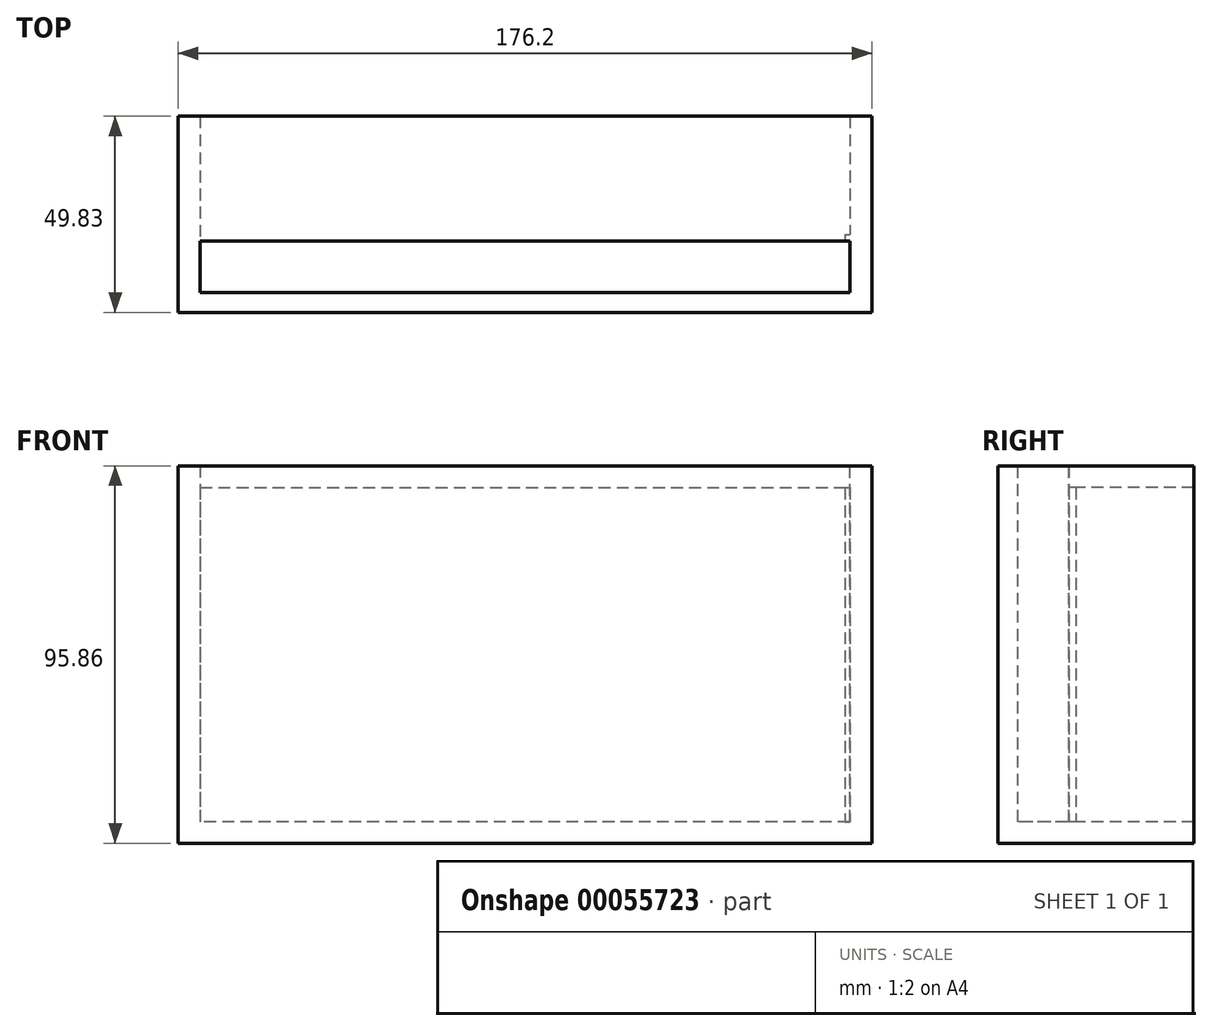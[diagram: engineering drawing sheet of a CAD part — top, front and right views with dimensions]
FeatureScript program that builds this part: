
annotation { "Feature Type Name" : "Feature", "Feature Type Description" : "" }
export const myFeature = defineFeature(function(context is Context, id is Id, definition is map)
    precondition{}
    {
        {
            var Q0;
            Q0=qCreatedBy(makeId("Front.planeOp"),FACE);
            var sketch = newSketch(context, id + "F0", { "sketchPlane" : qUnion([Q0])});
            skLineSegment(sketch, "E0.rect.bottom", {"start": v(82.5, 42.5) * mm, "end": v(-82.5, 42.5) * mm});
            skLineSegment(sketch, "E0.rect.top", {"start": v(82.5, -42.5) * mm, "end": v(-82.5, -42.5) * mm});
            skLineSegment(sketch, "E0.rect.left", {"start": v(82.5, 42.5) * mm, "end": v(82.5, -42.5) * mm});
            skLineSegment(sketch, "E0.rect.right", {"start": v(-82.5, 42.5) * mm, "end": v(-82.5, -42.5) * mm});
            skPoint(sketch, "E0.rect.middle", {"position": v(0, 0) * mm});
            skLineSegment(sketch, "E1.rect.bottom", {"start": v(88.1, 47.93) * mm, "end": v(-88.1, 47.93) * mm});
            skLineSegment(sketch, "E1.rect.top", {"start": v(88.1, -47.93) * mm, "end": v(-88.1, -47.93) * mm});
            skLineSegment(sketch, "E1.rect.left", {"start": v(88.1, 47.93) * mm, "end": v(88.1, -47.93) * mm});
            skLineSegment(sketch, "E1.rect.right", {"start": v(-88.1, 47.93) * mm, "end": v(-88.1, -47.93) * mm});
            skLineSegment(sketch, "E2", {"start": v(82.5, 42.5) * mm, "end": v(82.5, 47.93) * mm});
            skLineSegment(sketch, "E3", {"start": v(-82.5, 42.5) * mm, "end": v(-82.5, 47.93) * mm});
            skSolve(sketch);
        }
        {
            var Q0;
            Q0=makeQuery(id+"F0.imprint","IMPRINT",FACE,{"disambiguationData":[TD([[makeQuery(id+"F0.imprint","IMPRINT",EDGE,{"derivedFrom":sQuery(id+"F0.wireOp",EDGE,"E0.rect.bottom")}),-1.0]])]});
            var Q1;
            Q1=makeQuery(id+"F0.imprint","IMPRINT",FACE,{"disambiguationData":[TD([[makeQuery(id+"F0.imprint","IMPRINT",EDGE,{"derivedFrom":sQuery(id+"F0.wireOp",EDGE,"E0.rect.bottom")}),1.0]])]});
            var Q2;
            Q2=makeQuery(id+"F0.imprint","IMPRINT",FACE,{"disambiguationData":[TD([[makeQuery(id+"F0.imprint","IMPRINT",EDGE,{"derivedFrom":sQuery(id+"F0.wireOp",EDGE,"E0.rect.top")}),1.0]])]});
            extrude(context, id + "F1", {"entities" : qUnion([Q0, Q1, Q2]), "depth" : 5.08 * mm});
        }
        {
            var Q0;
            Q0=makeQuery(id+"F0.imprint","IMPRINT",FACE,{"disambiguationData":[TD([[makeQuery(id+"F0.imprint","IMPRINT",EDGE,{"derivedFrom":sQuery(id+"F0.wireOp",EDGE,"E0.rect.top")}),1.0]])]});
            extrude(context, id + "F2", {"entities" : qUnion([Q0]), "operationType" : NewBodyOperationType.ADD, "oppositeDirection" : true, "depth" : 13 * mm});
        }
        {
            var Q0;
            Q0=makeQuery(id+"F2.opExtrude","CAP_FACE",FACE,{"disambiguationData":[OSD([sQuery(id+"F0.wireOp",EDGE,"E0.rect.top"),sQuery(id+"F0.wireOp",EDGE,"E0.rect.left"),sQuery(id+"F0.wireOp",EDGE,"E0.rect.right"),sQuery(id+"F0.wireOp",EDGE,"E1.rect.bottom"),sQuery(id+"F0.wireOp",EDGE,"E1.rect.top"),sQuery(id+"F0.wireOp",EDGE,"E1.rect.left"),sQuery(id+"F0.wireOp",EDGE,"E1.rect.right"),sQuery(id+"F0.wireOp",EDGE,"E2"),sQuery(id+"F0.wireOp",EDGE,"E3")])],"isStart":false});
            var sketch = newSketch(context, id + "F3", { "sketchPlane" : qUnion([Q0])});
            skLineSegment(sketch, "E4.rect.bottom", {"start": v(82.5, 42.45) * mm, "end": v(-82.5, 42.45) * mm});
            skLineSegment(sketch, "E4.rect.top", {"start": v(82.5, -42.45) * mm, "end": v(-82.5, -42.45) * mm});
            skLineSegment(sketch, "E4.rect.left", {"start": v(82.5, 42.45) * mm, "end": v(82.5, -42.45) * mm});
            skLineSegment(sketch, "E4.rect.right", {"start": v(-82.5, 42.45) * mm, "end": v(-82.5, -42.45) * mm});
            skPoint(sketch, "E4.rect.middle", {"position": v(0, 0) * mm});
            skLineSegment(sketch, "E5.rect.bottom", {"start": v(88.1, 47.93) * mm, "end": v(-88.1, 47.93) * mm});
            skLineSegment(sketch, "E5.rect.top", {"start": v(88.1, -47.93) * mm, "end": v(-88.1, -47.93) * mm});
            skLineSegment(sketch, "E5.rect.left", {"start": v(88.1, 47.93) * mm, "end": v(88.1, -47.93) * mm});
            skLineSegment(sketch, "E5.rect.right", {"start": v(-88.1, 47.93) * mm, "end": v(-88.1, -47.93) * mm});
            skSolve(sketch);
        }
        {
            var Q0;
            {var subQ8=sQuery(id+"F3.wireOp",EDGE,"E4.rect.left");Q0=makeQuery(id+"F3.imprint","IMPRINT",FACE,{"disambiguationData":[TD([[makeQuery(id+"F3.imprint","IMPRINT",EDGE,{"derivedFrom":subQ8}),1.0]])]});}
            var Q1;
            {var subQ0=sQuery(id+"F3.wireOp",EDGE,"E4.rect.bottom");Q1=makeQuery(id+"F3.imprint","IMPRINT",FACE,{"disambiguationData":[TD([[makeQuery(id+"F3.imprint","IMPRINT",EDGE,{"derivedFrom":subQ0}),-1.0]])]});}
            extrude(context, id + "F4", {"entities" : qUnion([Q0, Q1]), "operationType" : NewBodyOperationType.ADD, "depth" : 31.75 * mm});
        }
        {
            var Q0;
            {var subQ0=sQuery(id+"F0.wireOp",EDGE,"E2");var subQ1=sQuery(id+"F0.wireOp",EDGE,"E0.rect.left");Q0=makeQuery(id+"F4.boolean.opBoolean","MERGE",FACE,{"derivedFrom":[makeQuery(id+"F2.opExtrude","SWEPT_FACE",FACE,{"disambiguationData":[OSD([subQ1,subQ0])]}),makeQuery(id+"F4.opExtrude","SWEPT_FACE",FACE,{"disambiguationData":[OSD([subQ1,subQ0,sQuery(id+"F3.wireOp",EDGE,"E4.rect.right")])]})]});}
            var sketch = newSketch(context, id + "F5", { "sketchPlane" : qUnion([Q0])});
            skLineSegment(sketch, "E6", {"start": v(-13, 47.93) * mm, "end": v(-13, -30.49) * mm});
            skLineSegment(sketch, "E7.bottom", {"start": v(-13, 45.2) * mm, "end": v(-14.73, 45.2) * mm});
            skLineSegment(sketch, "E7.top", {"start": v(-13, -42.5) * mm, "end": v(-14.73, -42.5) * mm});
            skLineSegment(sketch, "E7.left", {"start": v(-13, 45.2) * mm, "end": v(-13, -42.5) * mm});
            skLineSegment(sketch, "E7.right", {"start": v(-14.73, 45.2) * mm, "end": v(-14.73, -42.5) * mm});
            skSolve(sketch);
        }
        {
            var Q0;
            {var subQ1=sQuery(id+"F5.wireOp",EDGE,"E7.top");Q0=makeQuery(id+"F5.imprint","IMPRINT",FACE,{"disambiguationData":[TD([[makeQuery(id+"F5.imprint","IMPRINT",EDGE,{"derivedFrom":subQ1}),1.0]])]});}
            extrude(context, id + "F6", {"entities" : qUnion([Q0]), "operationType" : NewBodyOperationType.ADD, "depth" : 1.27 * mm});
        }
    });
